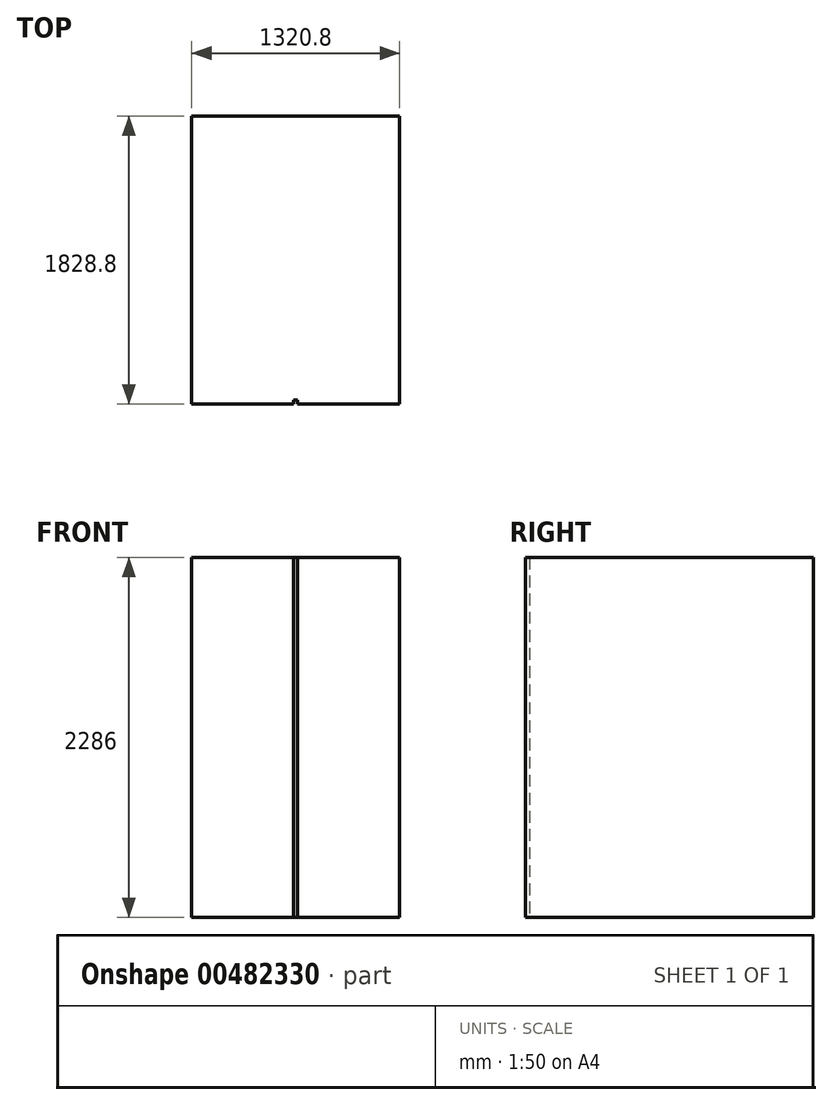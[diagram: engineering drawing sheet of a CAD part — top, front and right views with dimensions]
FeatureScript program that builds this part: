
annotation { "Feature Type Name" : "Feature", "Feature Type Description" : "" }
export const myFeature = defineFeature(function(context is Context, id is Id, definition is map)
    precondition{}
    {
        {
            var Q0;
            Q0=qCreatedBy(makeId("Top.planeOp"),FACE);
            var sketch = newSketch(context, id + "F0", { "sketchPlane" : qUnion([Q0])});
            skLineSegment(sketch, "E0.bottom", {"start": v(0, 0) * mm, "end": v(1320.8, 0) * mm});
            skLineSegment(sketch, "E0.top", {"start": v(0, 1828.8) * mm, "end": v(1320.8, 1828.8) * mm});
            skLineSegment(sketch, "E0.left", {"start": v(0, 0) * mm, "end": v(0, 1828.8) * mm});
            skLineSegment(sketch, "E0.right", {"start": v(1320.8, 0) * mm, "end": v(1320.8, 1828.8) * mm});
            skSolve(sketch);
        }
        {
            var Q0;
            Q0 = qSketchRegion(id + "F0", true);
            extrude(context, id + "F1", {"entities" : qUnion([Q0]), "depth" : 2286 * mm, "offsetDistance" : 25.4 * mm});
        }
        {
            var Q0;
            Q0=makeQuery(id+"F1.opExtrude","SWEPT_FACE",FACE,{"disambiguationData":[OSD([sQuery(id+"F0.wireOp",EDGE,"E0.bottom")])]});
            var sketch = newSketch(context, id + "F2", { "sketchPlane" : qUnion([Q0])});
            skLineSegment(sketch, "E1.bottom", {"start": v(647.7, 2286) * mm, "end": v(673.1, 2286) * mm});
            skLineSegment(sketch, "E1.top", {"start": v(647.7, 0) * mm, "end": v(673.1, 0) * mm});
            skLineSegment(sketch, "E1.left", {"start": v(647.7, 2286) * mm, "end": v(647.7, 0) * mm});
            skLineSegment(sketch, "E1.right", {"start": v(673.1, 2286) * mm, "end": v(673.1, 0) * mm});
            skPoint(sketch, "E2", {"position": v(660.4, 2286) * mm});
            skSolve(sketch);
        }
        {
            var Q0;
            Q0 = qSketchRegion(id + "F2", true);
            extrude(context, id + "F3", {"entities" : qUnion([Q0]), "operationType" : NewBodyOperationType.REMOVE, "oppositeDirection" : true, "depth" : 25.4 * mm, "offsetDistance" : 25.4 * mm});
        }
    });
